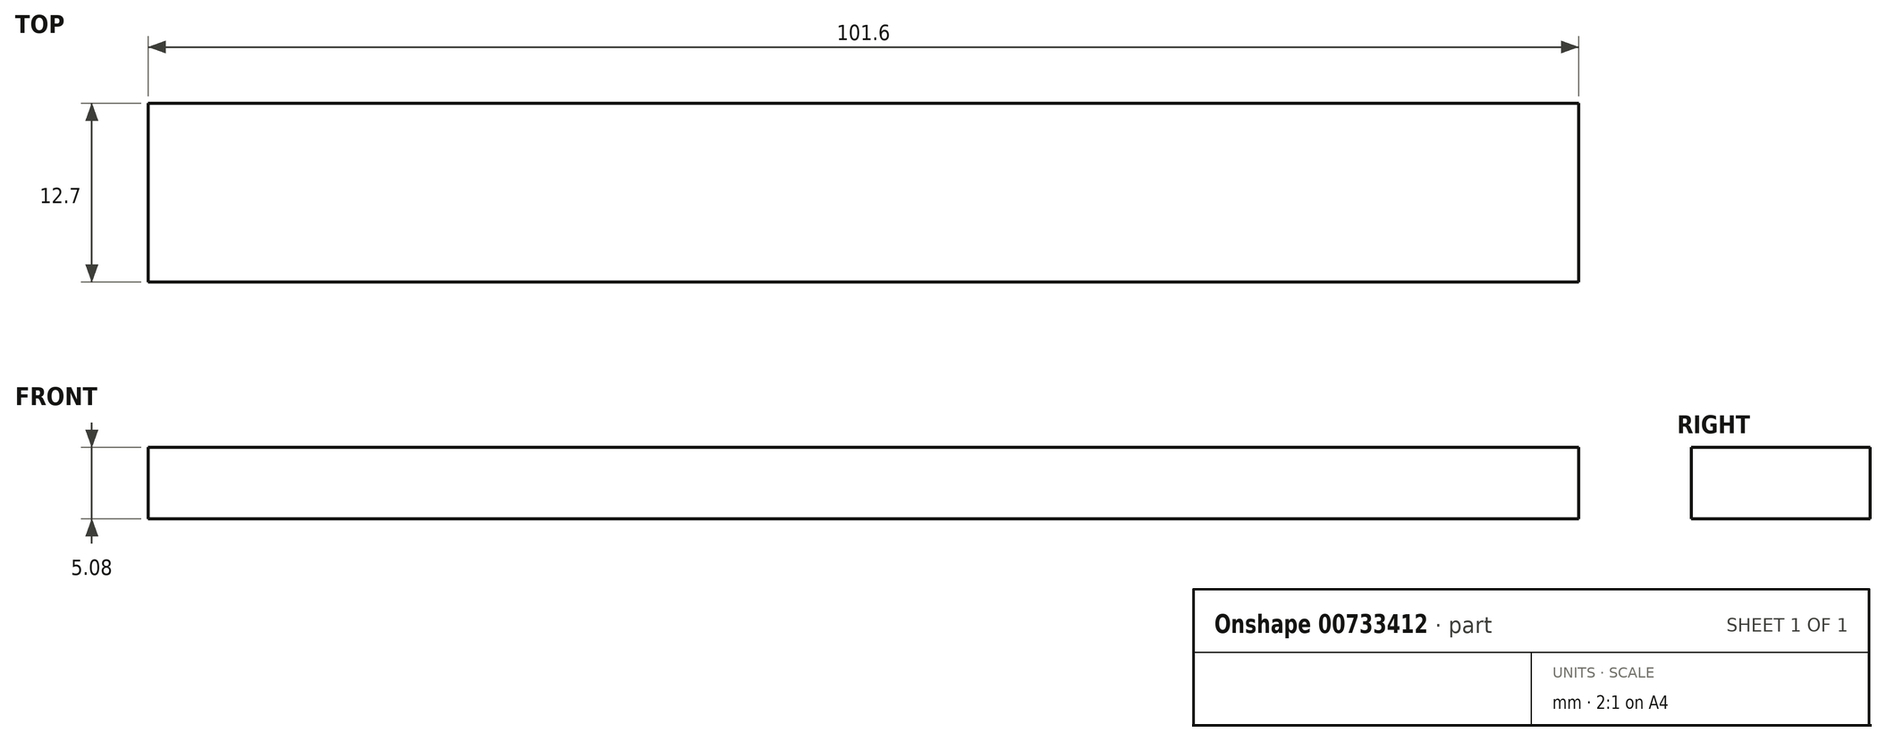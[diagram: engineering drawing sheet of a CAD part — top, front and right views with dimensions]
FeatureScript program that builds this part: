
annotation { "Feature Type Name" : "Feature", "Feature Type Description" : "" }
export const myFeature = defineFeature(function(context is Context, id is Id, definition is map)
    precondition{}
    {
        {
            var Q0;
            Q0=qCreatedBy(makeId("Front.planeOp"),FACE);
            var sketch = newSketch(context, id + "F0", { "sketchPlane" : qUnion([Q0])});
            skLineSegment(sketch, "E0.bottom", {"start": v(-35.64, 1.47) * mm, "end": v(65.96, 1.47) * mm});
            skLineSegment(sketch, "E0.top", {"start": v(-35.64, -3.6) * mm, "end": v(65.96, -3.6) * mm});
            skLineSegment(sketch, "E0.left", {"start": v(-35.64, 1.47) * mm, "end": v(-35.64, -3.6) * mm});
            skLineSegment(sketch, "E0.right", {"start": v(65.96, 1.47) * mm, "end": v(65.96, -3.6) * mm});
            skSolve(sketch);
        }
        {
            var Q0;
            Q0 = qSketchRegion(id + "F0", true);
            extrude(context, id + "F1", {"entities" : qUnion([Q0]), "depth" : 12.7 * mm, "offsetDistance" : 25.4 * mm});
        }
    });
